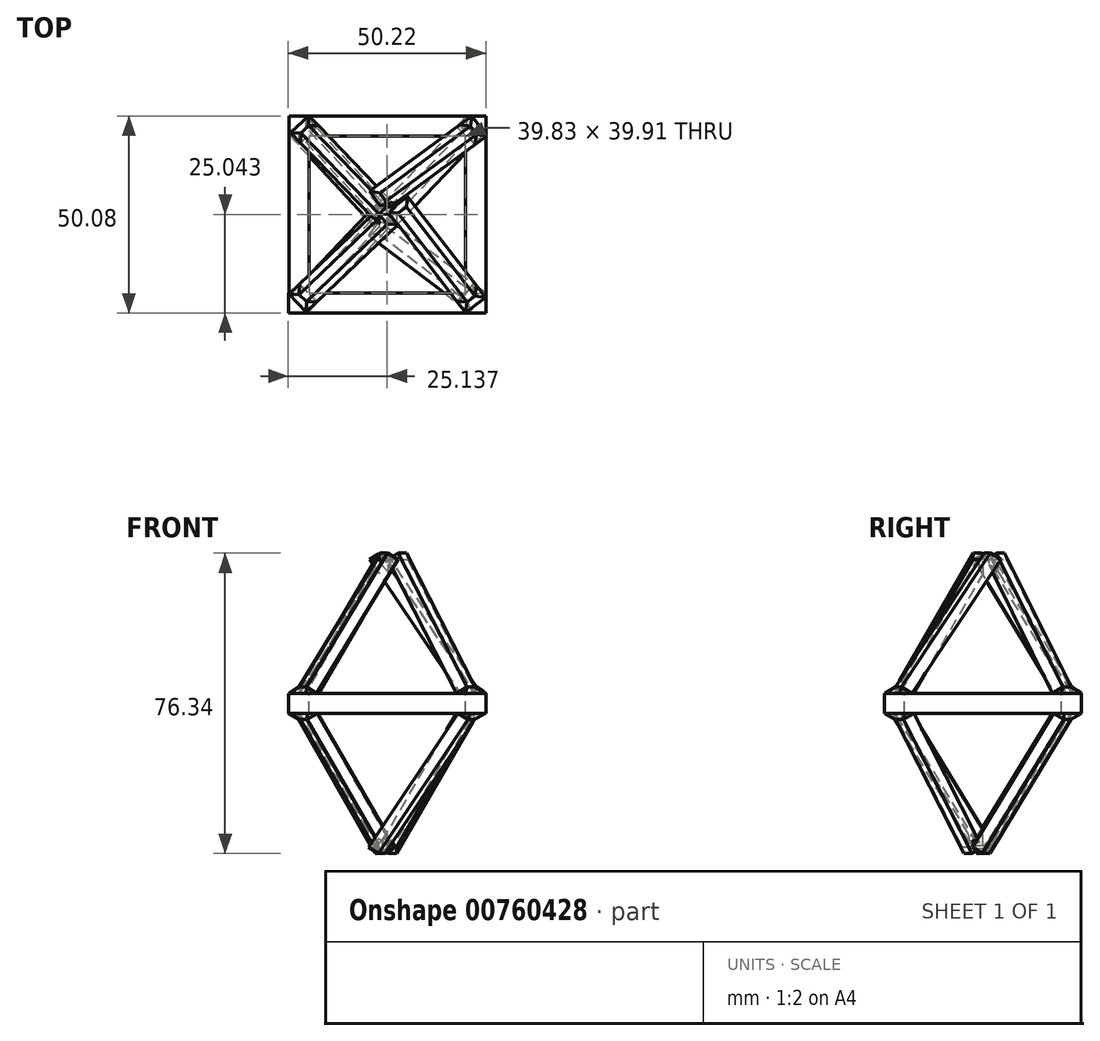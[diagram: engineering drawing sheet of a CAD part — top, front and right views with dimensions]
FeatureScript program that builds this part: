
annotation { "Feature Type Name" : "Feature", "Feature Type Description" : "" }
export const myFeature = defineFeature(function(context is Context, id is Id, definition is map)
    precondition{}
    {
        {
            var Q0;
            Q0=qCreatedBy(makeId("Top.planeOp"),FACE);
            var sketch = newSketch(context, id + "F0", { "sketchPlane" : qUnion([Q0])});
            skLineSegment(sketch, "E0.bottom", {"start": v(-22.5, 22.5) * mm, "end": v(22.5, 22.5) * mm});
            skLineSegment(sketch, "E0.top", {"start": v(-22.5, -22.5) * mm, "end": v(22.5, -22.5) * mm});
            skLineSegment(sketch, "E0.left", {"start": v(-22.5, 22.5) * mm, "end": v(-22.5, -22.5) * mm});
            skLineSegment(sketch, "E0.right", {"start": v(22.5, 22.5) * mm, "end": v(22.5, -22.5) * mm});
            skPoint(sketch, "E0.middle", {"position": v(0, 0) * mm});
            skSolve(sketch);
        }
        {
            var Q0;
            Q0=sQuery(id+"F0.wireOp",EDGE,"E0.left");
            extrude(context, id + "F1", {"bodyType" : ToolBodyType.SURFACE, "surfaceEntities" : qUnion([Q0]), "depth" : 5.08 * mm, "offsetDistance" : 25.4 * mm});
        }
        {
            var Q0;
            Q0=makeQuery(id+"F1.opExtrude","SWEPT_FACE",FACE,{"disambiguationData":[OSD([sQuery(id+"F0.wireOp",EDGE,"E0.left")])]});
            extrude(context, id + "F2", {"entities" : qUnion([Q0]), "depth" : 5.08 * mm, "offsetDistance" : 25.4 * mm});
        }
        {
            var Q0;
            Q0=makeQuery(id+"F1.opExtrude","SWEPT_FACE",FACE,{"disambiguationData":[OSD([sQuery(id+"F0.wireOp",EDGE,"E0.left")])]});
            var sketch = newSketch(context, id + "F3", { "sketchPlane" : qUnion([Q0])});
            skLineSegment(sketch, "E1", {"start": v(-22.5, 0) * mm, "end": v(-17.42, 0) * mm});
            skLineSegment(sketch, "E2", {"start": v(-17.42, 0) * mm, "end": v(-17.42, 5.08) * mm});
            skLineSegment(sketch, "E3", {"start": v(-17.42, 5.08) * mm, "end": v(-22.5, 5.08) * mm});
            skLineSegment(sketch, "E4", {"start": v(-22.5, 5.08) * mm, "end": v(-22.5, 0) * mm});
            skSolve(sketch);
        }
        {
            var Q0;
            Q0=makeQuery(id+"F3.imprint","IMPRINT",FACE,{"disambiguationData":[TD([[makeQuery(id+"F3.imprint","IMPRINT",EDGE,{"derivedFrom":sQuery(id+"F3.wireOp",EDGE,"E1")}),1.0]])]});
            extrude(context, id + "F4", {"entities" : qUnion([Q0]), "operationType" : NewBodyOperationType.ADD, "oppositeDirection" : true, "depth" : 45 * mm, "offsetDistance" : 25.4 * mm});
        }
        {
            var Q0;
            Q0=makeQuery(id+"F4.opExtrude","SWEPT_FACE",FACE,{"disambiguationData":[OSD([sQuery(id+"F3.wireOp",EDGE,"E2")])]});
            var sketch = newSketch(context, id + "F5", { "sketchPlane" : qUnion([Q0])});
            skLineSegment(sketch, "E5", {"start": v(22.5, 0) * mm, "end": v(17.33, 0) * mm});
            skLineSegment(sketch, "E6", {"start": v(17.33, 0) * mm, "end": v(17.33, 5.08) * mm});
            skLineSegment(sketch, "E7", {"start": v(17.33, 5.08) * mm, "end": v(22.5, 5.08) * mm});
            skLineSegment(sketch, "E8", {"start": v(22.5, 5.08) * mm, "end": v(22.5, 0) * mm});
            skSolve(sketch);
        }
        {
            var Q0;
            Q0=makeQuery(id+"F5.imprint","IMPRINT",FACE,{"disambiguationData":[TD([[makeQuery(id+"F5.imprint","IMPRINT",EDGE,{"derivedFrom":sQuery(id+"F5.wireOp",EDGE,"E5")}),-1.0]])]});
            extrude(context, id + "F6", {"entities" : qUnion([Q0]), "operationType" : NewBodyOperationType.ADD, "depth" : 45 * mm, "offsetDistance" : 25.4 * mm});
        }
        {
            var Q0;
            Q0=makeQuery(id+"F6.opExtrude","SWEPT_FACE",FACE,{"disambiguationData":[OSD([sQuery(id+"F5.wireOp",EDGE,"E6")])]});
            var sketch = newSketch(context, id + "F7", { "sketchPlane" : qUnion([Q0])});
            skLineSegment(sketch, "E9", {"start": v(27.58, 0) * mm, "end": v(22.5, 0) * mm});
            skLineSegment(sketch, "E10", {"start": v(22.5, 0) * mm, "end": v(22.5, 5.08) * mm});
            skLineSegment(sketch, "E11", {"start": v(22.5, 5.08) * mm, "end": v(27.58, 5.08) * mm});
            skLineSegment(sketch, "E12", {"start": v(27.58, 5.08) * mm, "end": v(27.58, 0) * mm});
            skSolve(sketch);
        }
        {
            var Q0;
            Q0=makeQuery(id+"F7.imprint","IMPRINT",FACE,{"disambiguationData":[TD([[makeQuery(id+"F7.imprint","IMPRINT",EDGE,{"derivedFrom":sQuery(id+"F7.wireOp",EDGE,"E9")}),-1.0]])]});
            extrude(context, id + "F8", {"entities" : qUnion([Q0]), "operationType" : NewBodyOperationType.ADD, "depth" : 45 * mm, "offsetDistance" : 25.4 * mm});
        }
        {
            var Q0;
            {var subQ0=sQuery(id+"F0.wireOp",EDGE,"E0.left");Q0=makeQuery(id+"F8.boolean.opBoolean","MERGE",FACE,{"derivedFrom":[makeQuery(id+"F6.boolean.opBoolean","MERGE",FACE,{"derivedFrom":[makeQuery(id+"F4.boolean.opBoolean","MERGE",FACE,{"derivedFrom":[makeQuery(id+"F2.opExtrude","SWEPT_FACE",FACE,{"disambiguationData":[OSD([subQ0]),TDD([makeQuery(id+"F1.opExtrude","CAP_EDGE",EDGE,{"disambiguationData":[OSD([subQ0])],"isStart":false})])]}),makeQuery(id+"F4.opExtrude","SWEPT_FACE",FACE,{"disambiguationData":[OSD([sQuery(id+"F3.wireOp",EDGE,"E3")])]})]}),makeQuery(id+"F6.opExtrude","SWEPT_FACE",FACE,{"disambiguationData":[OSD([sQuery(id+"F5.wireOp",EDGE,"E7")])]})]}),makeQuery(id+"F8.opExtrude","SWEPT_FACE",FACE,{"disambiguationData":[OSD([sQuery(id+"F7.wireOp",EDGE,"E11")])]})]});}
            var sketch = newSketch(context, id + "F9", { "sketchPlane" : qUnion([Q0])});
            skLineSegment(sketch, "E13", {"start": v(20.1, -20.6) * mm, "end": v(15.06, -24.5) * mm});
            skLineSegment(sketch, "E14", {"start": v(15.06, -24.5) * mm, "end": v(17.36, -27.47) * mm});
            skLineSegment(sketch, "E15", {"start": v(17.36, -27.47) * mm, "end": v(22.38, -23.59) * mm});
            skLineSegment(sketch, "E16", {"start": v(22.38, -23.59) * mm, "end": v(20.1, -20.6) * mm});
            skSolve(sketch);
        }
        {
            var Q0;
            Q0=makeQuery(id+"F9.imprint","IMPRINT",FACE,{"disambiguationData":[TD([[makeQuery(id+"F9.imprint","IMPRINT",EDGE,{"derivedFrom":sQuery(id+"F9.wireOp",EDGE,"E13")}),1.0]])]});
            extrude(context, id + "F10", {"entities" : qUnion([Q0]), "operationType" : NewBodyOperationType.ADD, "depth" : 5.08 * mm, "offsetDistance" : 25.4 * mm, "hasDraft" : true, "draftAngle" : 50 * degree, "draftPullDirection" : true});
        }
        {
            var Q0;
            Q0=makeQuery(id+"F10.opExtrude","SWEPT_FACE",FACE,{"disambiguationData":[OSD([sQuery(id+"F9.wireOp",EDGE,"E13")])]});
            extrude(context, id + "F11", {"entities" : qUnion([Q0]), "operationType" : NewBodyOperationType.ADD, "depth" : 44.45 * mm, "offsetDistance" : 25.4 * mm});
        }
        {
            var Q0;
            {var subQ0=sQuery(id+"F0.wireOp",EDGE,"E0.left");Q0=makeQuery(id+"F8.boolean.opBoolean","MERGE",FACE,{"derivedFrom":[makeQuery(id+"F6.boolean.opBoolean","MERGE",FACE,{"derivedFrom":[makeQuery(id+"F4.boolean.opBoolean","MERGE",FACE,{"derivedFrom":[makeQuery(id+"F2.opExtrude","SWEPT_FACE",FACE,{"disambiguationData":[OSD([subQ0]),TDD([makeQuery(id+"F1.opExtrude","CAP_EDGE",EDGE,{"disambiguationData":[OSD([subQ0])],"isStart":false})])]}),makeQuery(id+"F4.opExtrude","SWEPT_FACE",FACE,{"disambiguationData":[OSD([sQuery(id+"F3.wireOp",EDGE,"E3")])]})]}),makeQuery(id+"F6.opExtrude","SWEPT_FACE",FACE,{"disambiguationData":[OSD([sQuery(id+"F5.wireOp",EDGE,"E7")])]})]}),makeQuery(id+"F8.opExtrude","SWEPT_FACE",FACE,{"disambiguationData":[OSD([sQuery(id+"F7.wireOp",EDGE,"E11")])]})]});}
            var sketch = newSketch(context, id + "F12", { "sketchPlane" : qUnion([Q0])});
            skLineSegment(sketch, "E17", {"start": v(-24.86, -20.16) * mm, "end": v(-20.48, -24.76) * mm});
            skLineSegment(sketch, "E18", {"start": v(-20.48, -24.76) * mm, "end": v(-23.2, -27.35) * mm});
            skLineSegment(sketch, "E19", {"start": v(-23.2, -27.35) * mm, "end": v(-27.58, -22.75) * mm});
            skLineSegment(sketch, "E20", {"start": v(-27.58, -22.75) * mm, "end": v(-24.86, -20.16) * mm});
            skSolve(sketch);
        }
        {
            var Q0;
            Q0=makeQuery(id+"F12.imprint","IMPRINT",FACE,{"disambiguationData":[TD([[makeQuery(id+"F12.imprint","IMPRINT",EDGE,{"derivedFrom":sQuery(id+"F12.wireOp",EDGE,"E17")}),-1.0]])]});
            extrude(context, id + "F13", {"entities" : qUnion([Q0]), "operationType" : NewBodyOperationType.ADD, "depth" : 5.08 * mm, "offsetDistance" : 25.4 * mm, "hasDraft" : true, "draftAngle" : 50 * degree, "draftPullDirection" : true});
        }
        {
            var Q0;
            Q0=makeQuery(id+"F13.opExtrude","SWEPT_FACE",FACE,{"disambiguationData":[OSD([sQuery(id+"F12.wireOp",EDGE,"E17")])]});
            extrude(context, id + "F14", {"entities" : qUnion([Q0]), "operationType" : NewBodyOperationType.ADD, "depth" : 44.45 * mm, "offsetDistance" : 25.4 * mm});
        }
        {
            var Q0;
            {var subQ0=sQuery(id+"F0.wireOp",EDGE,"E0.left");Q0=makeQuery(id+"F8.boolean.opBoolean","MERGE",FACE,{"derivedFrom":[makeQuery(id+"F6.boolean.opBoolean","MERGE",FACE,{"derivedFrom":[makeQuery(id+"F4.boolean.opBoolean","MERGE",FACE,{"derivedFrom":[makeQuery(id+"F2.opExtrude","SWEPT_FACE",FACE,{"disambiguationData":[OSD([subQ0]),TDD([makeQuery(id+"F1.opExtrude","CAP_EDGE",EDGE,{"disambiguationData":[OSD([subQ0])],"isStart":false})])]}),makeQuery(id+"F4.opExtrude","SWEPT_FACE",FACE,{"disambiguationData":[OSD([sQuery(id+"F3.wireOp",EDGE,"E3")])]})]}),makeQuery(id+"F6.opExtrude","SWEPT_FACE",FACE,{"disambiguationData":[OSD([sQuery(id+"F5.wireOp",EDGE,"E7")])]})]}),makeQuery(id+"F8.opExtrude","SWEPT_FACE",FACE,{"disambiguationData":[OSD([sQuery(id+"F7.wireOp",EDGE,"E11")])]})]});}
            var sketch = newSketch(context, id + "F15", { "sketchPlane" : qUnion([Q0])});
            skLineSegment(sketch, "E21", {"start": v(15.94, 20.27) * mm, "end": v(19.7, 15.16) * mm});
            skLineSegment(sketch, "E22", {"start": v(19.7, 15.16) * mm, "end": v(22.73, 17.38) * mm});
            skLineSegment(sketch, "E23", {"start": v(22.73, 17.38) * mm, "end": v(18.97, 22.5) * mm});
            skLineSegment(sketch, "E24", {"start": v(18.97, 22.5) * mm, "end": v(15.94, 20.27) * mm});
            skSolve(sketch);
        }
        {
            var Q0;
            {var subQ8=sQuery(id+"F15.wireOp",EDGE,"E21");Q0=makeQuery(id+"F15.imprint","IMPRINT",FACE,{"disambiguationData":[TD([[makeQuery(id+"F15.imprint","IMPRINT",EDGE,{"derivedFrom":subQ8}),1.0]])]});}
            extrude(context, id + "F16", {"entities" : qUnion([Q0]), "operationType" : NewBodyOperationType.ADD, "depth" : 5.08 * mm, "offsetDistance" : 25.4 * mm, "hasDraft" : true, "draftAngle" : 50 * degree, "draftPullDirection" : true});
        }
        {
            var Q0;
            Q0=makeQuery(id+"F16.opExtrude","SWEPT_FACE",FACE,{"disambiguationData":[OSD([sQuery(id+"F15.wireOp",EDGE,"E21")])]});
            extrude(context, id + "F17", {"entities" : qUnion([Q0]), "operationType" : NewBodyOperationType.ADD, "depth" : 44.45 * mm, "offsetDistance" : 25.4 * mm});
        }
        {
            var Q0;
            {var subQ0=sQuery(id+"F9.wireOp",EDGE,"E16");var subQ1=sQuery(id+"F0.wireOp",EDGE,"E0.left");var subQ2=sQuery(id+"F9.wireOp",EDGE,"E13");var subQ3=makeQuery(id+"F2.opExtrude","SWEPT_FACE",FACE,{"disambiguationData":[OSD([subQ1]),TDD([makeQuery(id+"F1.opExtrude","CAP_EDGE",EDGE,{"disambiguationData":[OSD([subQ1])],"isStart":false})])]});var subQ4=sQuery(id+"F7.wireOp",EDGE,"E12");var subQ5=sQuery(id+"F7.wireOp",EDGE,"E11");var subQ6=makeQuery(id+"F8.opExtrude","SWEPT_FACE",FACE,{"disambiguationData":[OSD([subQ5])]});var subQ7=sQuery(id+"F7.wireOp",EDGE,"E10");var subQ8=sQuery(id+"F5.wireOp",EDGE,"E8");var subQ9=sQuery(id+"F12.wireOp",EDGE,"E18");var subQ10=sQuery(id+"F9.wireOp",EDGE,"E14");var subQ11=sQuery(id+"F3.wireOp",EDGE,"E3");var subQ12=makeQuery(id+"F4.opExtrude","SWEPT_FACE",FACE,{"disambiguationData":[OSD([subQ11])]});var subQ13=sQuery(id+"F5.wireOp",EDGE,"E7");var subQ14=makeQuery(id+"F6.opExtrude","SWEPT_FACE",FACE,{"disambiguationData":[OSD([subQ13])]});var subQ15=sQuery(id+"F3.wireOp",EDGE,"E2");var subQ16=sQuery(id+"F3.wireOp",EDGE,"E4");var subQ17=sQuery(id+"F5.wireOp",EDGE,"E6");var subQ18=sQuery(id+"F12.wireOp",EDGE,"E20");var subQ19=sQuery(id+"F12.wireOp",EDGE,"E17");Q0=makeQuery(id+"F16.boolean.opBoolean","SPLIT",FACE,{"disambiguationData":[TD([makeQuery(id+"F2.opExtrude","SWEPT_FACE",FACE,{"disambiguationData":[OSD([sQuery(id+"F0.wireOp",VERTEX,"E0.left.start")])]}),subQ3,makeQuery(id+"F2.opExtrude","CAP_FACE",FACE,{"disambiguationData":[OSD([subQ1])],"isStart":true}),makeQuery(id+"F2.opExtrude","CAP_FACE",FACE,{"disambiguationData":[OSD([subQ1])],"isStart":false}),makeQuery(id+"F4.opExtrude","CAP_FACE",FACE,{"disambiguationData":[OSD([sQuery(id+"F3.wireOp",EDGE,"E1"),subQ15,subQ11,subQ16])],"isStart":false}),makeQuery(id+"F4.opExtrude","SWEPT_FACE",FACE,{"disambiguationData":[OSD([subQ15])]}),subQ12,makeQuery(id+"F4.opExtrude","SWEPT_FACE",FACE,{"disambiguationData":[OSD([subQ16])]}),makeQuery(id+"F6.opExtrude","CAP_FACE",FACE,{"disambiguationData":[OSD([sQuery(id+"F5.wireOp",EDGE,"E5"),subQ17,subQ13,subQ8])],"isStart":false}),makeQuery(id+"F6.opExtrude","SWEPT_FACE",FACE,{"disambiguationData":[OSD([subQ17])]}),subQ14,makeQuery(id+"F6.opExtrude","SWEPT_FACE",FACE,{"disambiguationData":[OSD([subQ8])]}),makeQuery(id+"F8.opExtrude","CAP_FACE",FACE,{"disambiguationData":[OSD([sQuery(id+"F7.wireOp",EDGE,"E9"),subQ7,subQ5,subQ4])],"isStart":false}),makeQuery(id+"F8.opExtrude","SWEPT_FACE",FACE,{"disambiguationData":[OSD([subQ7])]}),subQ6,makeQuery(id+"F8.opExtrude","SWEPT_FACE",FACE,{"disambiguationData":[OSD([subQ4])]}),makeQuery(id+"F10.opExtrude","SWEPT_FACE",FACE,{"disambiguationData":[OSD([subQ10])]}),makeQuery(id+"F10.opExtrude","SWEPT_FACE",FACE,{"disambiguationData":[OSD([sQuery(id+"F9.wireOp",EDGE,"E15")])]}),makeQuery(id+"F10.opExtrude","SWEPT_FACE",FACE,{"disambiguationData":[OSD([subQ0])]}),makeQuery(id+"F11.opExtrude","SWEPT_FACE",FACE,{"disambiguationData":[OSD([subQ2,subQ0])]}),makeQuery(id+"F11.opExtrude","SWEPT_FACE",FACE,{"disambiguationData":[OSD([subQ2,subQ10])]}),makeQuery(id+"F11.opExtrude","SWEPT_FACE",FACE,{"disambiguationData":[OSD([subQ2])]}),makeQuery(id+"F13.opExtrude","SWEPT_FACE",FACE,{"disambiguationData":[OSD([subQ9])]}),makeQuery(id+"F13.opExtrude","SWEPT_FACE",FACE,{"disambiguationData":[OSD([sQuery(id+"F12.wireOp",EDGE,"E19")])]}),makeQuery(id+"F13.opExtrude","SWEPT_FACE",FACE,{"disambiguationData":[OSD([subQ18])]}),makeQuery(id+"F14.opExtrude","SWEPT_FACE",FACE,{"disambiguationData":[OSD([subQ19,subQ18])]}),makeQuery(id+"F14.opExtrude","SWEPT_FACE",FACE,{"disambiguationData":[OSD([subQ19,subQ9])]}),makeQuery(id+"F14.opExtrude","SWEPT_FACE",FACE,{"disambiguationData":[OSD([subQ19])]}),makeQuery(id+"F16.opExtrude","SWEPT_FACE",FACE,{"disambiguationData":[OSD([sQuery(id+"F15.wireOp",EDGE,"E21")])]}),makeQuery(id+"F16.opExtrude","SWEPT_FACE",FACE,{"disambiguationData":[OSD([sQuery(id+"F15.wireOp",EDGE,"E22")])]}),makeQuery(id+"F16.opExtrude","SWEPT_FACE",FACE,{"disambiguationData":[OSD([sQuery(id+"F15.wireOp",EDGE,"E23")])]}),makeQuery(id+"F16.opExtrude","SWEPT_FACE",FACE,{"disambiguationData":[OSD([sQuery(id+"F15.wireOp",EDGE,"E24")])]}),makeQuery(id+"F16.opExtrude","SWEPT_FACE",FACE,{"disambiguationData":[OSD([subQ11,subQ13,subQ8])]})])],"derivedFrom":makeQuery(id+"F8.boolean.opBoolean","MERGE",FACE,{"derivedFrom":[makeQuery(id+"F6.boolean.opBoolean","MERGE",FACE,{"derivedFrom":[makeQuery(id+"F4.boolean.opBoolean","MERGE",FACE,{"derivedFrom":[subQ3,subQ12]}),subQ14]}),subQ6]})});}
            var sketch = newSketch(context, id + "F18", { "sketchPlane" : qUnion([Q0])});
            skLineSegment(sketch, "E25", {"start": v(-24.55, 15.6) * mm, "end": v(-19.98, 20) * mm});
            skLineSegment(sketch, "E26", {"start": v(-19.98, 20) * mm, "end": v(-22.5, 22.61) * mm});
            skLineSegment(sketch, "E27", {"start": v(-22.5, 22.61) * mm, "end": v(-27.07, 18.2) * mm});
            skLineSegment(sketch, "E28", {"start": v(-27.07, 18.2) * mm, "end": v(-24.55, 15.6) * mm});
            skSolve(sketch);
        }
        {
            var Q0;
            {var subQ9=sQuery(id+"F18.wireOp",EDGE,"E25");Q0=makeQuery(id+"F18.imprint","IMPRINT",FACE,{"disambiguationData":[TD([[makeQuery(id+"F18.imprint","IMPRINT",EDGE,{"derivedFrom":subQ9}),1.0]])]});}
            extrude(context, id + "F19", {"entities" : qUnion([Q0]), "operationType" : NewBodyOperationType.ADD, "depth" : 5.08 * mm, "offsetDistance" : 25.4 * mm, "hasDraft" : true, "draftAngle" : 50 * degree, "draftPullDirection" : true});
        }
        {
            var Q0;
            Q0=makeQuery(id+"F19.opExtrude","SWEPT_FACE",FACE,{"disambiguationData":[OSD([sQuery(id+"F18.wireOp",EDGE,"E25")])]});
            extrude(context, id + "F20", {"entities" : qUnion([Q0]), "operationType" : NewBodyOperationType.ADD, "depth" : 44.45 * mm, "offsetDistance" : 25.4 * mm});
        }
        {
            var Q0;
            {var subQ0=sQuery(id+"F0.wireOp",EDGE,"E0.left");Q0=makeQuery(id+"F8.boolean.opBoolean","MERGE",FACE,{"derivedFrom":[makeQuery(id+"F6.boolean.opBoolean","MERGE",FACE,{"derivedFrom":[makeQuery(id+"F4.boolean.opBoolean","MERGE",FACE,{"derivedFrom":[makeQuery(id+"F2.opExtrude","SWEPT_FACE",FACE,{"disambiguationData":[OSD([subQ0]),TDD([makeQuery(id+"F1.opExtrude","CAP_EDGE",EDGE,{"disambiguationData":[OSD([subQ0])],"isStart":true})])]}),makeQuery(id+"F4.opExtrude","SWEPT_FACE",FACE,{"disambiguationData":[OSD([sQuery(id+"F3.wireOp",EDGE,"E1")])]})]}),makeQuery(id+"F6.opExtrude","SWEPT_FACE",FACE,{"disambiguationData":[OSD([sQuery(id+"F5.wireOp",EDGE,"E5")])]})]}),makeQuery(id+"F8.opExtrude","SWEPT_FACE",FACE,{"disambiguationData":[OSD([sQuery(id+"F7.wireOp",EDGE,"E9")])]})]});}
            var sketch = newSketch(context, id + "F21", { "sketchPlane" : qUnion([Q0])});
            skLineSegment(sketch, "E29", {"start": v(-24.83, 20.45) * mm, "end": v(-20.22, 24.82) * mm});
            skLineSegment(sketch, "E30", {"start": v(-20.22, 24.82) * mm, "end": v(-22.81, 27.55) * mm});
            skLineSegment(sketch, "E31", {"start": v(-22.81, 27.55) * mm, "end": v(-27.42, 23.18) * mm});
            skLineSegment(sketch, "E32", {"start": v(-27.42, 23.18) * mm, "end": v(-24.83, 20.45) * mm});
            skSolve(sketch);
        }
        {
            var Q0;
            Q0=makeQuery(id+"F21.imprint","IMPRINT",FACE,{"disambiguationData":[TD([[makeQuery(id+"F21.imprint","IMPRINT",EDGE,{"derivedFrom":sQuery(id+"F21.wireOp",EDGE,"E29")}),1.0]])]});
            extrude(context, id + "F22", {"entities" : qUnion([Q0]), "operationType" : NewBodyOperationType.ADD, "depth" : 5.08 * mm, "offsetDistance" : 25.4 * mm, "hasDraft" : true, "draftAngle" : 50 * degree, "draftPullDirection" : true});
        }
        {
            var Q0;
            Q0=makeQuery(id+"F22.opExtrude","SWEPT_FACE",FACE,{"disambiguationData":[OSD([sQuery(id+"F21.wireOp",EDGE,"E29")])]});
            extrude(context, id + "F23", {"entities" : qUnion([Q0]), "operationType" : NewBodyOperationType.ADD, "depth" : 44.45 * mm, "offsetDistance" : 25.4 * mm});
        }
        {
            var Q0;
            {var subQ0=sQuery(id+"F0.wireOp",EDGE,"E0.left");Q0=makeQuery(id+"F8.boolean.opBoolean","MERGE",FACE,{"derivedFrom":[makeQuery(id+"F6.boolean.opBoolean","MERGE",FACE,{"derivedFrom":[makeQuery(id+"F4.boolean.opBoolean","MERGE",FACE,{"derivedFrom":[makeQuery(id+"F2.opExtrude","SWEPT_FACE",FACE,{"disambiguationData":[OSD([subQ0]),TDD([makeQuery(id+"F1.opExtrude","CAP_EDGE",EDGE,{"disambiguationData":[OSD([subQ0])],"isStart":true})])]}),makeQuery(id+"F4.opExtrude","SWEPT_FACE",FACE,{"disambiguationData":[OSD([sQuery(id+"F3.wireOp",EDGE,"E1")])]})]}),makeQuery(id+"F6.opExtrude","SWEPT_FACE",FACE,{"disambiguationData":[OSD([sQuery(id+"F5.wireOp",EDGE,"E5")])]})]}),makeQuery(id+"F8.opExtrude","SWEPT_FACE",FACE,{"disambiguationData":[OSD([sQuery(id+"F7.wireOp",EDGE,"E9")])]})]});}
            var sketch = newSketch(context, id + "F24", { "sketchPlane" : qUnion([Q0])});
            skLineSegment(sketch, "E33", {"start": v(-25.16, -15.16) * mm, "end": v(-20.5, -19.48) * mm});
            skLineSegment(sketch, "E34", {"start": v(-20.5, -19.48) * mm, "end": v(-23.07, -22.23) * mm});
            skLineSegment(sketch, "E35", {"start": v(-23.07, -22.23) * mm, "end": v(-27.72, -17.91) * mm});
            skLineSegment(sketch, "E36", {"start": v(-27.72, -17.91) * mm, "end": v(-25.16, -15.16) * mm});
            skSolve(sketch);
        }
        {
            var Q0;
            Q0 = qSketchRegion(id + "F24", true);
            extrude(context, id + "F25", {"entities" : qUnion([Q0]), "operationType" : NewBodyOperationType.ADD, "depth" : 5.08 * mm, "offsetDistance" : 25.4 * mm, "hasDraft" : true, "draftAngle" : 50 * degree, "draftPullDirection" : true});
        }
        {
            var Q0;
            Q0=makeQuery(id+"F25.opExtrude","SWEPT_FACE",FACE,{"disambiguationData":[OSD([sQuery(id+"F24.wireOp",EDGE,"E33")])]});
            extrude(context, id + "F26", {"entities" : qUnion([Q0]), "operationType" : NewBodyOperationType.ADD, "depth" : 44.45 * mm, "offsetDistance" : 25.4 * mm});
        }
        {
            var Q0;
            {var subQ0=sQuery(id+"F0.wireOp",EDGE,"E0.left");Q0=makeQuery(id+"F8.boolean.opBoolean","MERGE",FACE,{"derivedFrom":[makeQuery(id+"F6.boolean.opBoolean","MERGE",FACE,{"derivedFrom":[makeQuery(id+"F4.boolean.opBoolean","MERGE",FACE,{"derivedFrom":[makeQuery(id+"F2.opExtrude","SWEPT_FACE",FACE,{"disambiguationData":[OSD([subQ0]),TDD([makeQuery(id+"F1.opExtrude","CAP_EDGE",EDGE,{"disambiguationData":[OSD([subQ0])],"isStart":true})])]}),makeQuery(id+"F4.opExtrude","SWEPT_FACE",FACE,{"disambiguationData":[OSD([sQuery(id+"F3.wireOp",EDGE,"E1")])]})]}),makeQuery(id+"F6.opExtrude","SWEPT_FACE",FACE,{"disambiguationData":[OSD([sQuery(id+"F5.wireOp",EDGE,"E5")])]})]}),makeQuery(id+"F8.opExtrude","SWEPT_FACE",FACE,{"disambiguationData":[OSD([sQuery(id+"F7.wireOp",EDGE,"E9")])]})]});}
            var sketch = newSketch(context, id + "F27", { "sketchPlane" : qUnion([Q0])});
            skLineSegment(sketch, "E37", {"start": v(19.59, -15.35) * mm, "end": v(15, -19.74) * mm});
            skLineSegment(sketch, "E38", {"start": v(15, -19.74) * mm, "end": v(17.6, -22.45) * mm});
            skLineSegment(sketch, "E39", {"start": v(17.6, -22.45) * mm, "end": v(22.19, -18.06) * mm});
            skLineSegment(sketch, "E40", {"start": v(22.19, -18.06) * mm, "end": v(19.59, -15.35) * mm});
            skSolve(sketch);
        }
        {
            var Q0;
            Q0=makeQuery(id+"F27.imprint","IMPRINT",FACE,{"disambiguationData":[TD([[makeQuery(id+"F27.imprint","IMPRINT",EDGE,{"derivedFrom":sQuery(id+"F27.wireOp",EDGE,"E37")}),1.0]])]});
            extrude(context, id + "F28", {"entities" : qUnion([Q0]), "operationType" : NewBodyOperationType.ADD, "depth" : 5.08 * mm, "offsetDistance" : 25.4 * mm, "hasDraft" : true, "draftAngle" : 50 * degree, "draftPullDirection" : true});
        }
        {
            var Q0;
            Q0=makeQuery(id+"F28.opExtrude","SWEPT_FACE",FACE,{"disambiguationData":[OSD([sQuery(id+"F27.wireOp",EDGE,"E37")])]});
            extrude(context, id + "F29", {"entities" : qUnion([Q0]), "operationType" : NewBodyOperationType.ADD, "depth" : 44.45 * mm, "offsetDistance" : 25.4 * mm});
        }
        {
            var Q0;
            {var subQ0=sQuery(id+"F0.wireOp",EDGE,"E0.left");Q0=makeQuery(id+"F8.boolean.opBoolean","MERGE",FACE,{"derivedFrom":[makeQuery(id+"F6.boolean.opBoolean","MERGE",FACE,{"derivedFrom":[makeQuery(id+"F4.boolean.opBoolean","MERGE",FACE,{"derivedFrom":[makeQuery(id+"F2.opExtrude","SWEPT_FACE",FACE,{"disambiguationData":[OSD([subQ0]),TDD([makeQuery(id+"F1.opExtrude","CAP_EDGE",EDGE,{"disambiguationData":[OSD([subQ0])],"isStart":true})])]}),makeQuery(id+"F4.opExtrude","SWEPT_FACE",FACE,{"disambiguationData":[OSD([sQuery(id+"F3.wireOp",EDGE,"E1")])]})]}),makeQuery(id+"F6.opExtrude","SWEPT_FACE",FACE,{"disambiguationData":[OSD([sQuery(id+"F5.wireOp",EDGE,"E5")])]})]}),makeQuery(id+"F8.opExtrude","SWEPT_FACE",FACE,{"disambiguationData":[OSD([sQuery(id+"F7.wireOp",EDGE,"E9")])]})]});}
            var sketch = newSketch(context, id + "F30", { "sketchPlane" : qUnion([Q0])});
            skLineSegment(sketch, "E41", {"start": v(15.37, 25.12) * mm, "end": v(19.22, 20.07) * mm});
            skLineSegment(sketch, "E42", {"start": v(19.22, 20.07) * mm, "end": v(22.2, 22.35) * mm});
            skLineSegment(sketch, "E43", {"start": v(22.2, 22.35) * mm, "end": v(18.36, 27.4) * mm});
            skLineSegment(sketch, "E44", {"start": v(18.36, 27.4) * mm, "end": v(15.37, 25.12) * mm});
            skSolve(sketch);
        }
        {
            var Q0;
            Q0=makeQuery(id+"F30.imprint","IMPRINT",FACE,{"disambiguationData":[TD([[makeQuery(id+"F30.imprint","IMPRINT",EDGE,{"derivedFrom":sQuery(id+"F30.wireOp",EDGE,"E41")}),1.0]])]});
            extrude(context, id + "F31", {"entities" : qUnion([Q0]), "operationType" : NewBodyOperationType.ADD, "depth" : 5.08 * mm, "offsetDistance" : 25.4 * mm, "hasDraft" : true, "draftAngle" : 50 * degree, "draftPullDirection" : true});
        }
        {
            var Q0;
            Q0=makeQuery(id+"F31.opExtrude","SWEPT_FACE",FACE,{"disambiguationData":[OSD([sQuery(id+"F30.wireOp",EDGE,"E41")])]});
            extrude(context, id + "F32", {"entities" : qUnion([Q0]), "operationType" : NewBodyOperationType.ADD, "depth" : 44.45 * mm, "offsetDistance" : 25.4 * mm});
        }
    });
